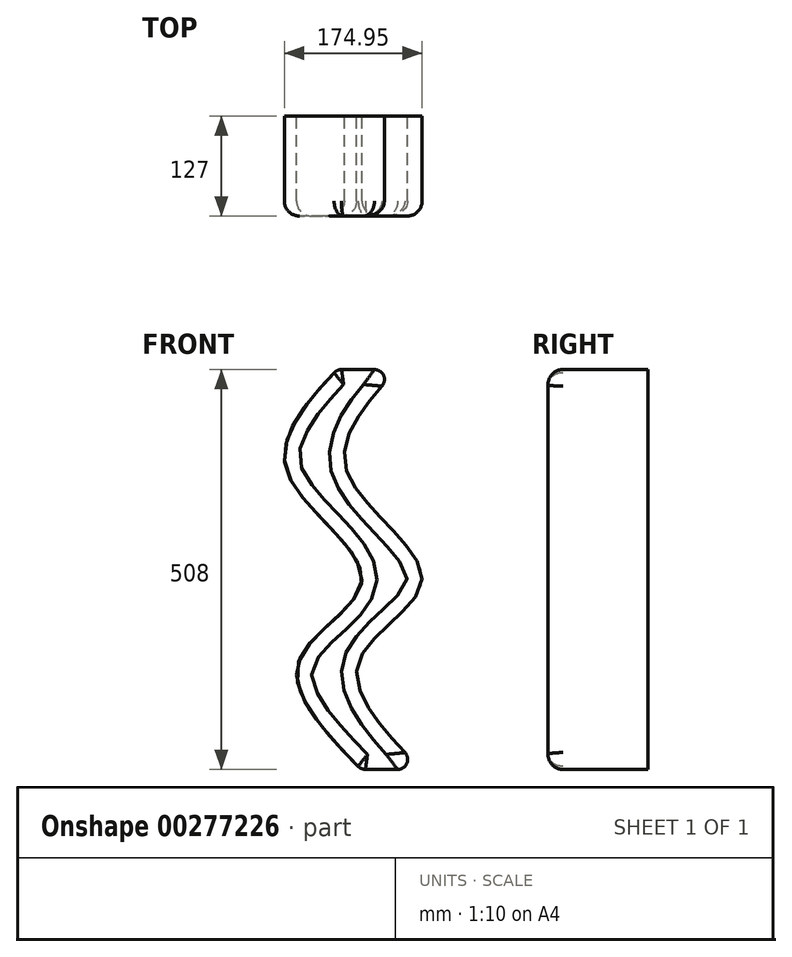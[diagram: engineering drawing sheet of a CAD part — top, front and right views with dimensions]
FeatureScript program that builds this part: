
annotation { "Feature Type Name" : "Feature", "Feature Type Description" : "" }
export const myFeature = defineFeature(function(context is Context, id is Id, definition is map)
    precondition{}
    {
        {
            var Q0;
            Q0=qCreatedBy(makeId("Front.planeOp"),FACE);
            var sketch = newSketch(context, id + "F0", { "sketchPlane" : qUnion([Q0])});
            skFitSpline(sketch, "E0", {"points": [v(-78.93, 247.75) * mm, v(-142.45, 117.9) * mm, v(-47.17, -18.48) * mm, v(-127.5, -122.17) * mm, v(-48.38, -260.25) * mm], "startDerivative": vector(-483.06, -524.92) * mm, "endDerivative": vector(549.76, -567.1) * mm});
            skFitSpline(sketch, "E1", {"points": [v(-2.73, 247.75) * mm, v(-66.25, 117.9) * mm, v(29.03, -18.48) * mm, v(-51.3, -122.17) * mm, v(27.82, -260.25) * mm], "startDerivative": vector(-483.06, -524.92) * mm, "endDerivative": vector(549.76, -567.1) * mm});
            skLineSegment(sketch, "E2", {"start": v(-2.73, 247.75) * mm, "end": v(-78.93, 247.75) * mm});
            skLineSegment(sketch, "E3", {"start": v(-48.38, -260.25) * mm, "end": v(27.82, -260.25) * mm});
            skSolve(sketch);
        }
        {
            var Q0;
            Q0 = qSketchRegion(id + "F0", true);
            extrude(context, id + "F1", {"entities" : qUnion([Q0]), "depth" : 127 * mm});
        }
        {
            var Q0;
            Q0=makeQuery(id+"F1.opExtrude","CAP_EDGE",EDGE,{"disambiguationData":[OSD([sQuery(id+"F0.wireOp",EDGE,"E2")])],"isStart":false});
            var Q1;
            Q1=makeQuery(id+"F1.opExtrude","CAP_EDGE",EDGE,{"disambiguationData":[OSD([sQuery(id+"F0.wireOp",EDGE,"E3")])],"isStart":false});
            var Q2;
            Q2=makeQuery(id+"F1.opExtrude","CAP_EDGE",EDGE,{"disambiguationData":[OSD([sQuery(id+"F0.wireOp",EDGE,"E0")])],"isStart":false});
            var Q3;
            Q3=makeQuery(id+"F1.opExtrude","CAP_EDGE",EDGE,{"disambiguationData":[OSD([sQuery(id+"F0.wireOp",EDGE,"E1")])],"isStart":false});
            fillet(context, id + "F2", {"entities" : qUnion([Q0, Q1, Q2, Q3]), "radius" : 19.05 * mm, "tangentPropagation" : true, "allowEdgeOverflow" : false});
        }
        {
            var Q0;
            Q0=makeQuery(id+"F1.opExtrude","SWEPT_EDGE",EDGE,{"disambiguationData":[OSD([sQuery(id+"F0.wireOp",EDGE,"E1"),sQuery(id+"F0.wireOp",EDGE,"E2")])]});
            var Q1;
            Q1=makeQuery(id+"F1.opExtrude","SWEPT_EDGE",EDGE,{"disambiguationData":[OSD([sQuery(id+"F0.wireOp",EDGE,"E0"),sQuery(id+"F0.wireOp",EDGE,"E2")])]});
            var Q2;
            Q2=makeQuery(id+"F1.opExtrude","SWEPT_EDGE",EDGE,{"disambiguationData":[OSD([sQuery(id+"F0.wireOp",EDGE,"E0"),sQuery(id+"F0.wireOp",EDGE,"E3")])]});
            var Q3;
            Q3=makeQuery(id+"F1.opExtrude","SWEPT_EDGE",EDGE,{"disambiguationData":[OSD([sQuery(id+"F0.wireOp",EDGE,"E1"),sQuery(id+"F0.wireOp",EDGE,"E3")])]});
            fillet(context, id + "F3", {"entities" : qUnion([Q0, Q1, Q2, Q3]), "radius" : 12.7 * mm, "tangentPropagation" : true, "allowEdgeOverflow" : false});
        }
    });
